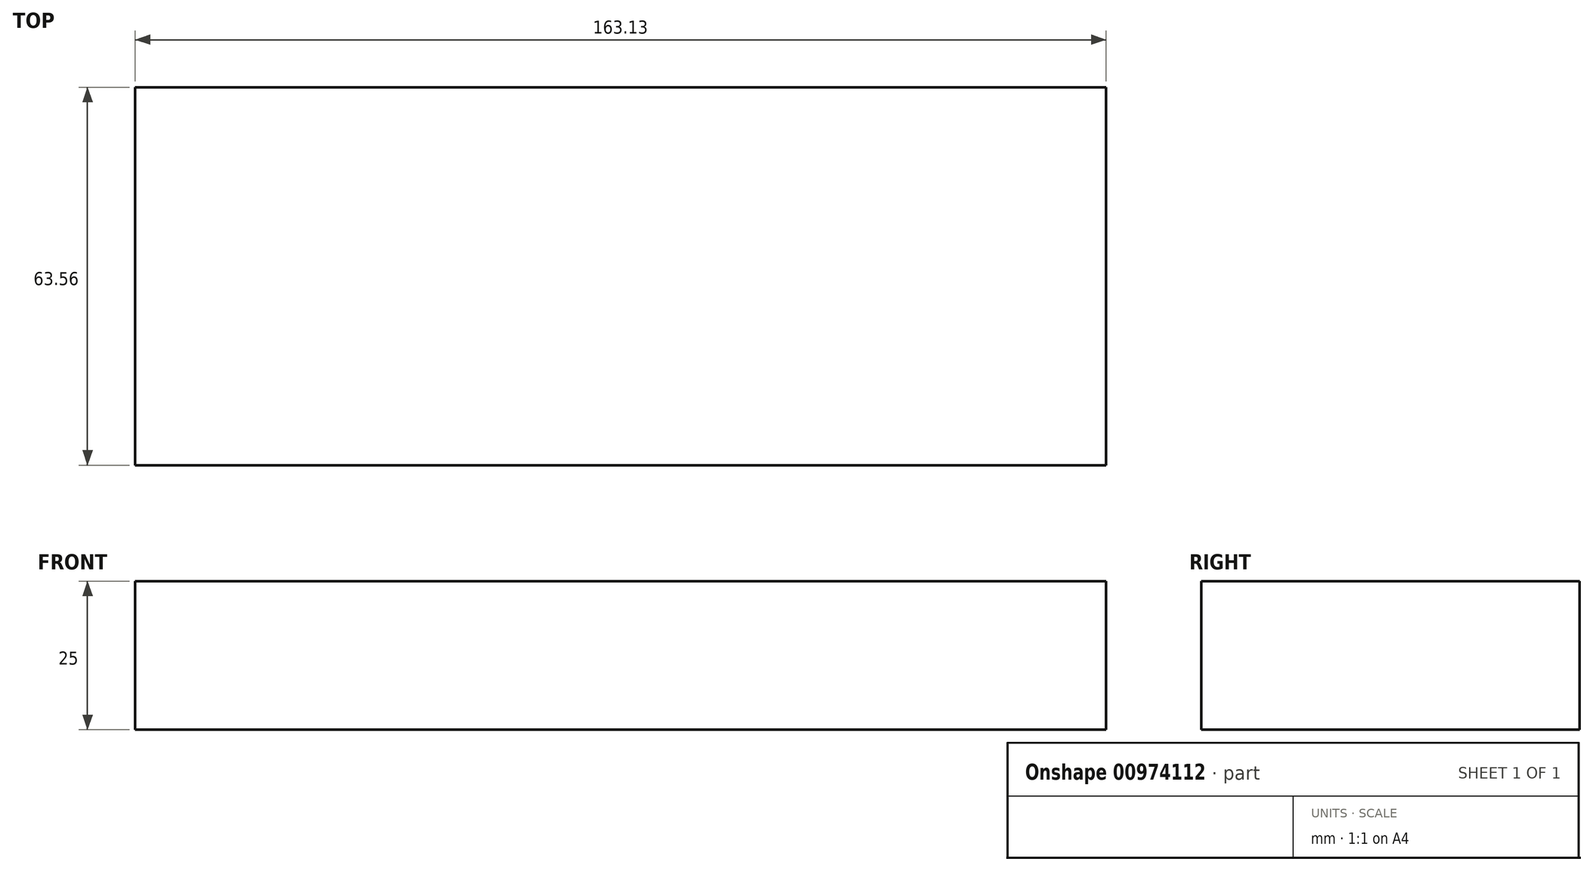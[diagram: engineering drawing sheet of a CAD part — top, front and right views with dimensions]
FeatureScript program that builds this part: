
annotation { "Feature Type Name" : "Feature", "Feature Type Description" : "" }
export const myFeature = defineFeature(function(context is Context, id is Id, definition is map)
    precondition{}
    {
        {
            var Q0;
            Q0=qCreatedBy(makeId("Top.planeOp"),FACE);
            var sketch = newSketch(context, id + "F0", { "sketchPlane" : qUnion([Q0])});
            skLineSegment(sketch, "E0.bottom", {"start": v(-86.49, 0) * mm, "end": v(76.64, 0) * mm});
            skLineSegment(sketch, "E0.top", {"start": v(-86.49, -63.56) * mm, "end": v(76.64, -63.56) * mm});
            skLineSegment(sketch, "E0.left", {"start": v(-86.49, 0) * mm, "end": v(-86.49, -63.56) * mm});
            skLineSegment(sketch, "E0.right", {"start": v(76.64, 0) * mm, "end": v(76.64, -63.56) * mm});
            skSolve(sketch);
        }
        {
            var Q0;
            Q0=makeQuery(id+"F0.imprint","IMPRINT",FACE,{"disambiguationData":[TD([[makeQuery(id+"F0.imprint","IMPRINT",EDGE,{"derivedFrom":sQuery(id+"F0.wireOp",EDGE,"E0.bottom")}),-1.0]])]});
            extrude(context, id + "F1", {"entities" : qUnion([Q0]), "depth" : 25 * mm, "offsetDistance" : 25 * mm});
        }
    });
